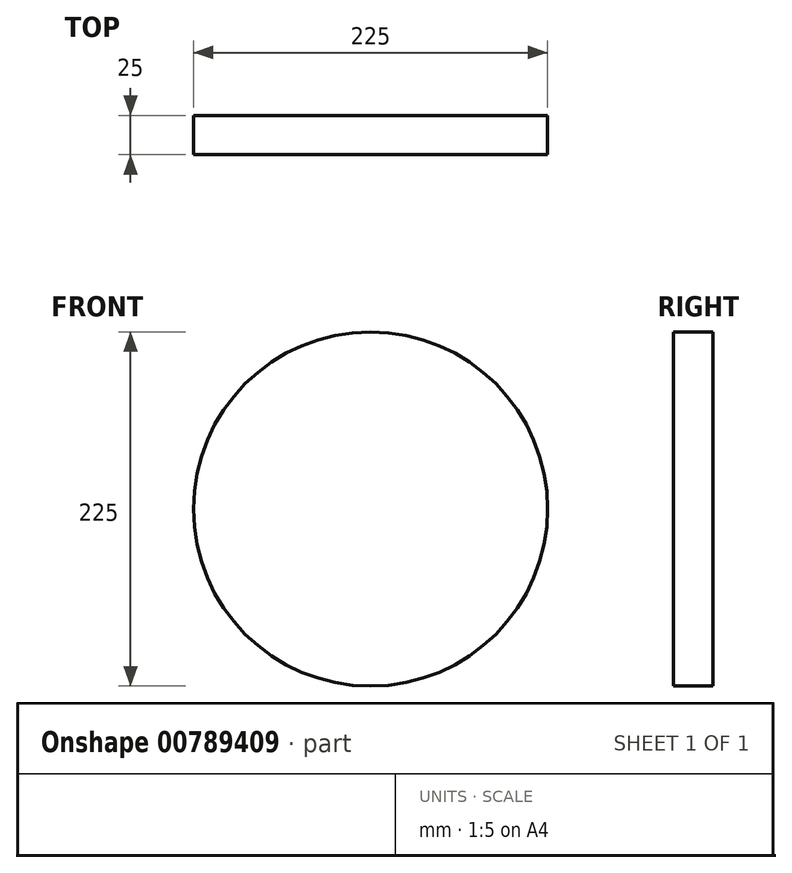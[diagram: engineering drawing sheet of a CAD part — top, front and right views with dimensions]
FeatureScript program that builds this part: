
annotation { "Feature Type Name" : "Feature", "Feature Type Description" : "" }
export const myFeature = defineFeature(function(context is Context, id is Id, definition is map)
    precondition{}
    {
        {
            var Q0;
            Q0=qCreatedBy(makeId("Front.planeOp"),FACE);
            var sketch = newSketch(context, id + "F0", { "sketchPlane" : qUnion([Q0])});
            skCircle(sketch, "E0", {"center": v(0, 0) * mm, "radius": 112.5 * mm});
            skSolve(sketch);
        }
        {
            var Q0;
            Q0=qCreatedBy(makeId("Right.planeOp"),FACE);
            var sketch = newSketch(context, id + "F1", { "sketchPlane" : qUnion([Q0])});
            skCircle(sketch, "E1", {"center": v(0, 0) * mm, "radius": 112.5 * mm});
            skSolve(sketch);
        }
        {
            var Q0;
            Q0=qCreatedBy(makeId("Top.planeOp"),FACE);
            var sketch = newSketch(context, id + "F2", { "sketchPlane" : qUnion([Q0])});
            skCircle(sketch, "E2", {"center": v(0, 0) * mm, "radius": 112.5 * mm});
            skSolve(sketch);
        }
        {
            var Q0;
            Q0=sQuery(id+"F1.wireOp",EDGE,"E1");
            extrude(context, id + "F3", {"bodyType" : ToolBodyType.SURFACE, "surfaceEntities" : qUnion([Q0]), "endBound" : BoundingType.SYMMETRIC, "depth" : 25 * mm, "offsetDistance" : 25 * mm});
        }
        {
            var Q0;
            Q0=sQuery(id+"F2.wireOp",EDGE,"E2");
            extrude(context, id + "F4", {"bodyType" : ToolBodyType.SURFACE, "surfaceEntities" : qUnion([Q0]), "endBound" : BoundingType.SYMMETRIC, "depth" : 25 * mm, "offsetDistance" : 25 * mm});
        }
        {
            var Q0;
            Q0=makeQuery(id+"F0.imprint","IMPRINT",FACE,{"disambiguationData":[TD([[makeQuery(id+"F0.imprint","IMPRINT",EDGE,{"derivedFrom":sQuery(id+"F0.wireOp",EDGE,"E0")}),1.0]])]});
            extrude(context, id + "F5", {"entities" : qUnion([Q0]), "endBound" : BoundingType.SYMMETRIC, "depth" : 25 * mm, "offsetDistance" : 25 * mm});
        }
    });
